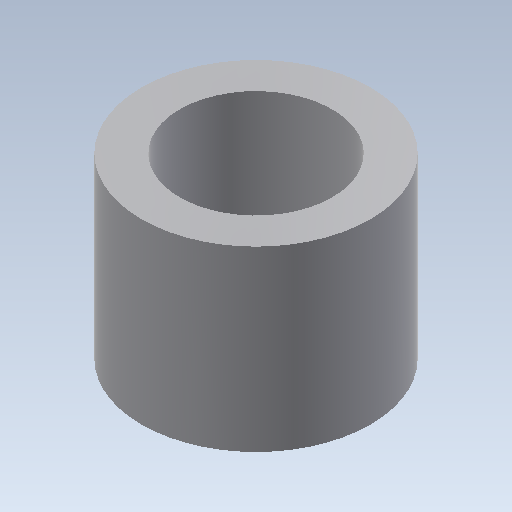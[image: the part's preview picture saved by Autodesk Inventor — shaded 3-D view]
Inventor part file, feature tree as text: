
AUTODESK INVENTOR PART (.ipt)
format: ipt  version: 2020 (Build 240168000, 168)  size: 89,600 bytes
history: native  units: mm
features: extrude x1, sketch x1
ambient origin geometry x8: Origin, YZ Plane, XZ Plane, XY Plane, X Axis, Y Axis, Z Axis, Center Point
bodies: Solid1 (feature_tree)
feature tree (2):
  extrude  "Extrusion1"  Depth=3.5mm
  sketch  "Sketch1"  dims[d0=4.5mm d1=3.0mm d2=3.5mm d3=0.0mm]
